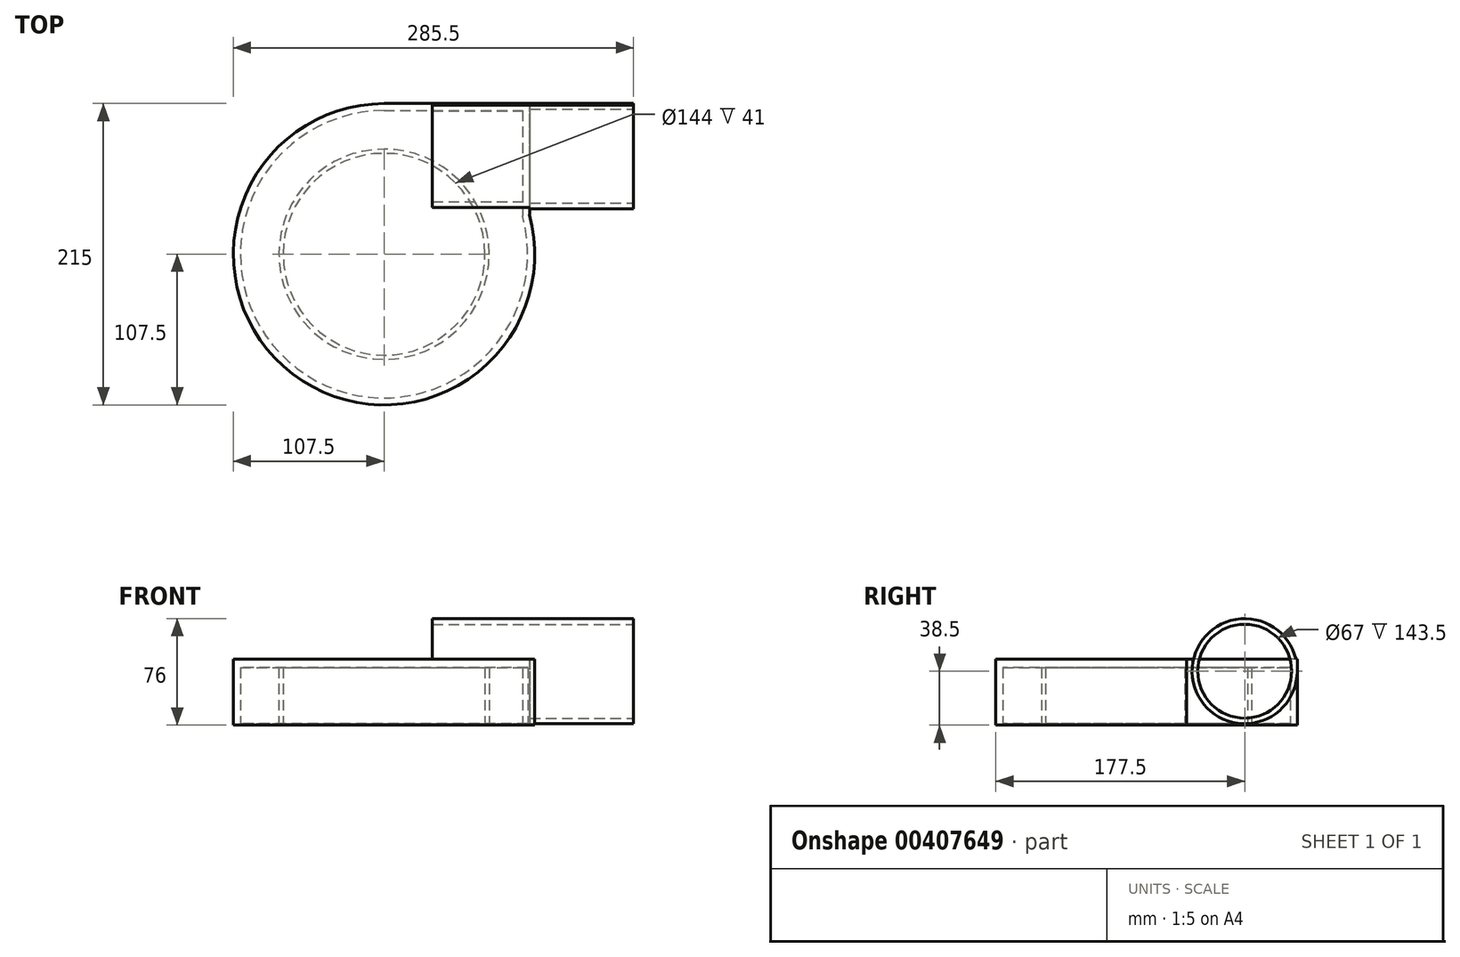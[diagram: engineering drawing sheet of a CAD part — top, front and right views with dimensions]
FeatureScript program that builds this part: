
annotation { "Feature Type Name" : "Feature", "Feature Type Description" : "" }
export const myFeature = defineFeature(function(context is Context, id is Id, definition is map)
    precondition{}
    {
        {
            var Q0;
            Q0=qCreatedBy(makeId("Top.planeOp"),FACE);
            var sketch = newSketch(context, id + "F0", { "sketchPlane" : qUnion([Q0])});
            skArc(sketch, "E0", {"start": v(0, 107.5) * mm, "mid": v(-65.16, -85.5) * mm, "end": v(103.65, 28.5) * mm});
            skLineSegment(sketch, "E1", {"start": v(0, 107.5) * mm, "end": v(178, 107.5) * mm});
            skLineSegment(sketch, "E2", {"start": v(178, 107.5) * mm, "end": v(178, 28.5) * mm});
            skLineSegment(sketch, "E3", {"start": v(178, 28.5) * mm, "end": v(103.65, 28.5) * mm});
            skSolve(sketch);
        }
        {
            var Q0;
            Q0=makeQuery(id+"F0.imprint","IMPRINT",FACE,{"disambiguationData":[TD([[makeQuery(id+"F0.imprint","IMPRINT",EDGE,{"derivedFrom":sQuery(id+"F0.wireOp",EDGE,"E0")}),1.0]])]});
            extrude(context, id + "F1", {"entities" : qUnion([Q0]), "depth" : 46 * mm});
        }
        {
            var Q0;
            Q0=makeQuery(id+"F1.opExtrude","SWEPT_FACE",FACE,{"disambiguationData":[OSD([sQuery(id+"F0.wireOp",EDGE,"E2")])]});
            var sketch = newSketch(context, id + "F2", { "sketchPlane" : qUnion([Q0])});
            skCircle(sketch, "E4", {"center": v(70, 37.5) * mm, "radius": 33.5 * mm});
            skCircle(sketch, "E5", {"center": v(70, 37.5) * mm, "radius": 37.5 * mm});
            skSolve(sketch);
        }
        {
            var Q0;
            {var subQ1=sQuery(id+"F0.wireOp",EDGE,"E2");var subQ6=makeQuery(id+"F1.opExtrude","SWEPT_EDGE",EDGE,{"disambiguationData":[OSD([subQ1,sQuery(id+"F0.wireOp",EDGE,"E3")])]});Q0=makeQuery(id+"F2.imprint","IMPRINT",FACE,{"disambiguationData":[TD([[makeQuery(id+"F2.imprint","IMPRINT",EDGE,{"derivedFrom":subQ6}),1.0]])]});}
            var Q1;
            {var subQ0=sQuery(id+"F2.wireOp",EDGE,"E5");var subQ1=sQuery(id+"F0.wireOp",EDGE,"E2");var subQ4=makeQuery(id+"F1.opExtrude","CAP_EDGE",EDGE,{"disambiguationData":[OSD([subQ1])],"isStart":true});var subQ5=makeQuery(id+"F2.imprint","INTERSECT",VERTEX,{"derivedFrom":[subQ4,subQ0]});Q1=makeQuery(id+"F2.imprint","IMPRINT",FACE,{"disambiguationData":[TD([[makeQuery(id+"F2.imprint","IMPRINT",EDGE,{"disambiguationData":[TD([[subQ5,-1.0]])],"derivedFrom":subQ0}),-1.0]])]});}
            var Q2;
            {var subQ0=sQuery(id+"F2.wireOp",EDGE,"E4");var subQ1=makeQuery(id+"F1.opExtrude","CAP_EDGE",EDGE,{"disambiguationData":[OSD([sQuery(id+"F0.wireOp",EDGE,"E2")])],"isStart":false});var subQ2=makeQuery(id+"F2.imprint","INTERSECT",VERTEX,{"disambiguationData":[OD(0.0)],"derivedFrom":[subQ1,subQ0]});Q2=makeQuery(id+"F2.imprint","IMPRINT",FACE,{"disambiguationData":[TD([[makeQuery(id+"F2.imprint","IMPRINT",EDGE,{"disambiguationData":[TD([[subQ2,1.0]])],"derivedFrom":subQ0}),1.0]])]});}
            extrude(context, id + "F3", {"entities" : qUnion([Q0, Q1, Q2]), "operationType" : NewBodyOperationType.REMOVE, "oppositeDirection" : true, "depth" : 74 * mm});
        }
        {
            var Q0;
            {var subQ0=sQuery(id+"F2.wireOp",EDGE,"E4");var subQ1=makeQuery(id+"F1.opExtrude","CAP_EDGE",EDGE,{"disambiguationData":[OSD([sQuery(id+"F0.wireOp",EDGE,"E2")])],"isStart":false});var subQ2=makeQuery(id+"F2.imprint","INTERSECT",VERTEX,{"disambiguationData":[OD(0.0)],"derivedFrom":[subQ1,subQ0]});Q0=makeQuery(id+"F2.imprint","IMPRINT",FACE,{"disambiguationData":[TD([[makeQuery(id+"F2.imprint","IMPRINT",EDGE,{"disambiguationData":[TD([[subQ2,-1.0]])],"derivedFrom":subQ0}),-1.0]])]});}
            extrude(context, id + "F4", {"entities" : qUnion([Q0]), "operationType" : NewBodyOperationType.ADD, "oppositeDirection" : true, "depth" : 143.5 * mm});
        }
        {
            var Q0;
            Q0=makeQuery(id+"F1.opExtrude","CAP_FACE",FACE,{"disambiguationData":[OSD([sQuery(id+"F0.wireOp",EDGE,"E0"),sQuery(id+"F0.wireOp",EDGE,"E1"),sQuery(id+"F0.wireOp",EDGE,"E2"),sQuery(id+"F0.wireOp",EDGE,"E3")])],"isStart":true});
            var sketch = newSketch(context, id + "F5", { "sketchPlane" : qUnion([Q0])});
            skCircle(sketch, "E6", {"center": v(0, 0) * mm, "radius": 75 * mm});
            skArc(sketch, "E7.0", {"start": v(0, -102.5) * mm, "mid": v(-62.13, 81.52) * mm, "end": v(98.83, -27.17) * mm});
            skLineSegment(sketch, "E8", {"start": v(0, -102.5) * mm, "end": v(98.83, -102.5) * mm});
            skLineSegment(sketch, "E9", {"start": v(98.83, -102.5) * mm, "end": v(98.83, -27.17) * mm});
            skCircle(sketch, "E10.0", {"center": v(0, 0) * mm, "radius": 72 * mm});
            skSolve(sketch);
        }
        {
            var Q0;
            Q0=makeQuery(id+"F5.imprint","IMPRINT",FACE,{"disambiguationData":[TD([[makeQuery(id+"F5.imprint","IMPRINT",EDGE,{"derivedFrom":sQuery(id+"F5.wireOp",EDGE,"E6")}),-1.0]])]});
            var Q1;
            Q1=makeQuery(id+"F5.imprint","IMPRINT",FACE,{"disambiguationData":[TD([[makeQuery(id+"F5.imprint","IMPRINT",EDGE,{"derivedFrom":sQuery(id+"F5.wireOp",EDGE,"E10.0")}),1.0]])]});
            extrude(context, id + "F6", {"entities" : qUnion([Q0, Q1]), "operationType" : NewBodyOperationType.REMOVE, "oppositeDirection" : true, "depth" : 40 * mm});
        }
        {
            var Q0;
            {var subQ1=sQuery(id+"F0.wireOp",EDGE,"E2");var subQ2=sQuery(id+"F0.wireOp",EDGE,"E1");var subQ4=sQuery(id+"F0.wireOp",EDGE,"E3");var subQ5=sQuery(id+"F0.wireOp",EDGE,"E0");Q0=makeQuery(id+"F6.boolean.opBoolean","SPLIT",FACE,{"disambiguationData":[TD([makeQuery(id+"F1.opExtrude","SWEPT_FACE",FACE,{"disambiguationData":[OSD([subQ5])]})])],"derivedFrom":makeQuery(id+"F1.opExtrude","CAP_FACE",FACE,{"disambiguationData":[OSD([subQ5,subQ2,subQ1,subQ4])],"isStart":true})});}
            var sketch = newSketch(context, id + "F7", { "sketchPlane" : qUnion([Q0])});
            skArc(sketch, "E11.0", {"start": v(0, -107.5) * mm, "mid": v(-65.16, 85.5) * mm, "end": v(103.65, -28.5) * mm});
            skLineSegment(sketch, "E12.0", {"start": v(104, -70) * mm, "end": v(104, -28.5) * mm});
            skLineSegment(sketch, "E13.0", {"start": v(104, -107.5) * mm, "end": v(104, -70) * mm});
            skLineSegment(sketch, "E14.0", {"start": v(0, -107.5) * mm, "end": v(104, -107.5) * mm});
            skCircle(sketch, "E15.0", {"center": v(0, 0) * mm, "radius": 72 * mm});
            skSolve(sketch);
        }
        {
            var Q0;
            Q0=makeQuery(id+"F7.imprint","IMPRINT",FACE,{"disambiguationData":[TD([[makeQuery(id+"F7.imprint","IMPRINT",EDGE,{"derivedFrom":sQuery(id+"F7.wireOp",EDGE,"E15.0")}),-1.0]])]});
            var Q1;
            Q1=makeQuery(id+"F7.imprint","IMPRINT",FACE,{"disambiguationData":[TD([[makeQuery(id+"F7.imprint","IMPRINT",EDGE,{"derivedFrom":sQuery(id+"F7.wireOp",EDGE,"E11.0")}),-1.0]])]});
            extrude(context, id + "F8", {"entities" : qUnion([Q0, Q1]), "operationType" : NewBodyOperationType.ADD, "depth" : 1 * mm});
        }
    });
